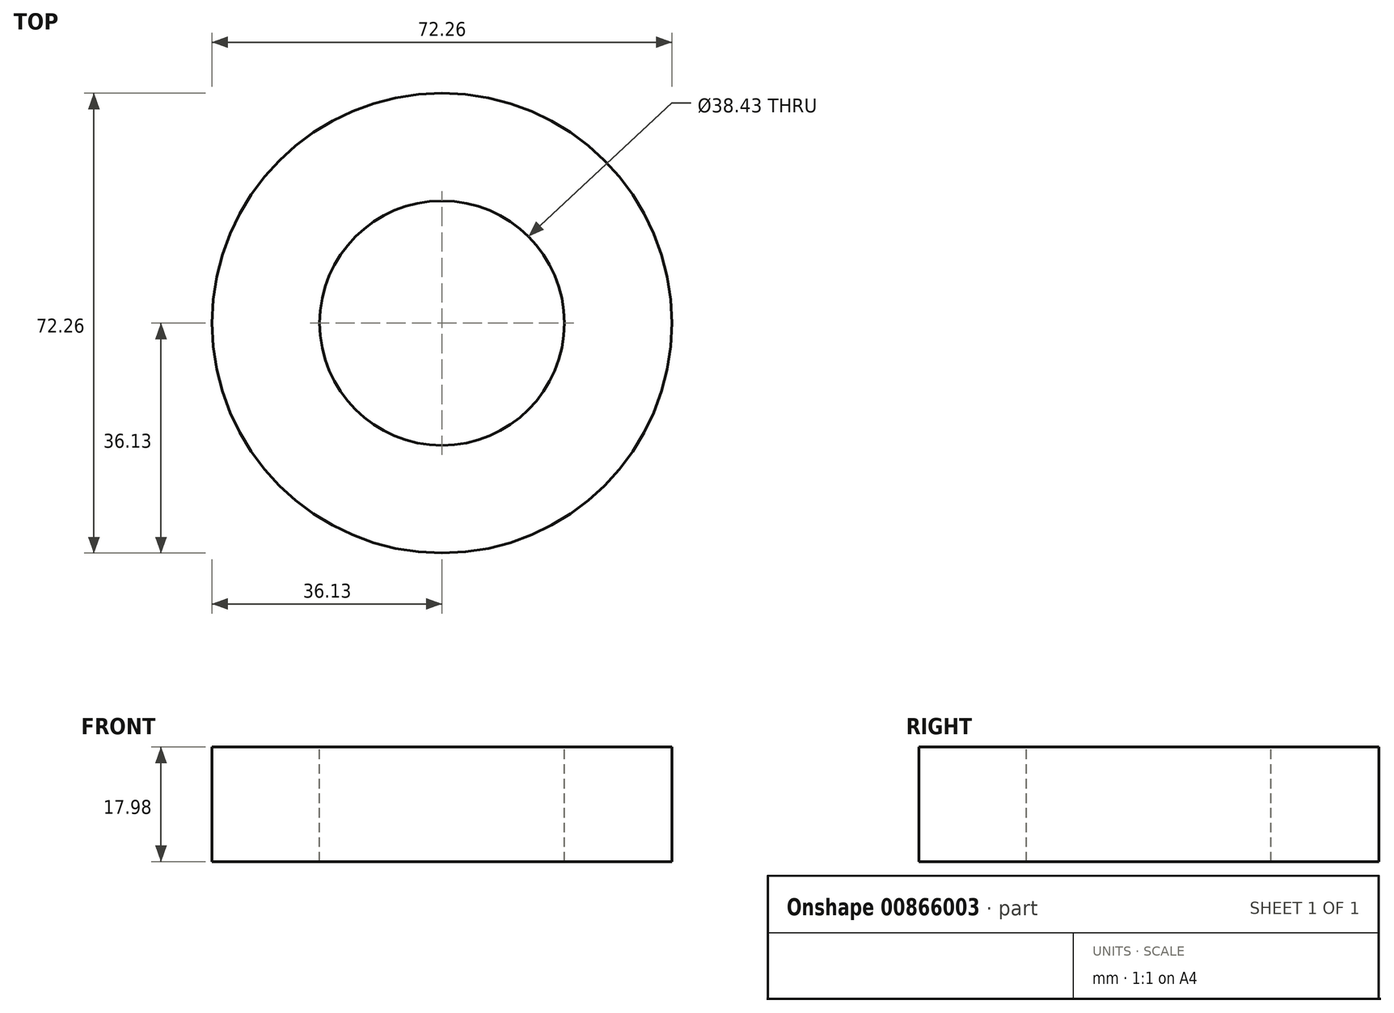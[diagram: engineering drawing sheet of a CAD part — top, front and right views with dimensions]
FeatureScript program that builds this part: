
annotation { "Feature Type Name" : "Feature", "Feature Type Description" : "" }
export const myFeature = defineFeature(function(context is Context, id is Id, definition is map)
    precondition{}
    {
        {
            var Q0;
            Q0=qCreatedBy(makeId("Front.planeOp"),FACE);
            var sketch = newSketch(context, id + "F0", { "sketchPlane" : qUnion([Q0])});
            skLineSegment(sketch, "E0", {"start": v(19.22, 0) * mm, "end": v(19.22, 17.98) * mm});
            skLineSegment(sketch, "E1", {"start": v(19.22, 17.98) * mm, "end": v(36.13, 17.98) * mm});
            skLineSegment(sketch, "E2", {"start": v(36.13, 17.98) * mm, "end": v(36.13, 0) * mm});
            skLineSegment(sketch, "E3", {"start": v(0, 133.57) * mm, "end": v(0, -132.63) * mm});
            skLineSegment(sketch, "E4", {"start": v(36.13, 0) * mm, "end": v(19.22, 0) * mm});
            skSolve(sketch);
        }
        {
            var Q0;
            Q0=makeQuery(id+"F0.imprint","IMPRINT",FACE,{"disambiguationData":[TD([[makeQuery(id+"F0.imprint","IMPRINT",EDGE,{"derivedFrom":sQuery(id+"F0.wireOp",EDGE,"E0")}),-1.0]])]});
            var Q1;
            Q1=sQuery(id+"F0.wireOp",EDGE,"E3");
            revolve(context, id + "F1", {"surfaceOperationType" : NewSurfaceOperationType.NEW, "entities" : qUnion([Q0]), "axis" : qUnion([Q1]), "revolveType" : RevolveType.FULL});
        }
    });
